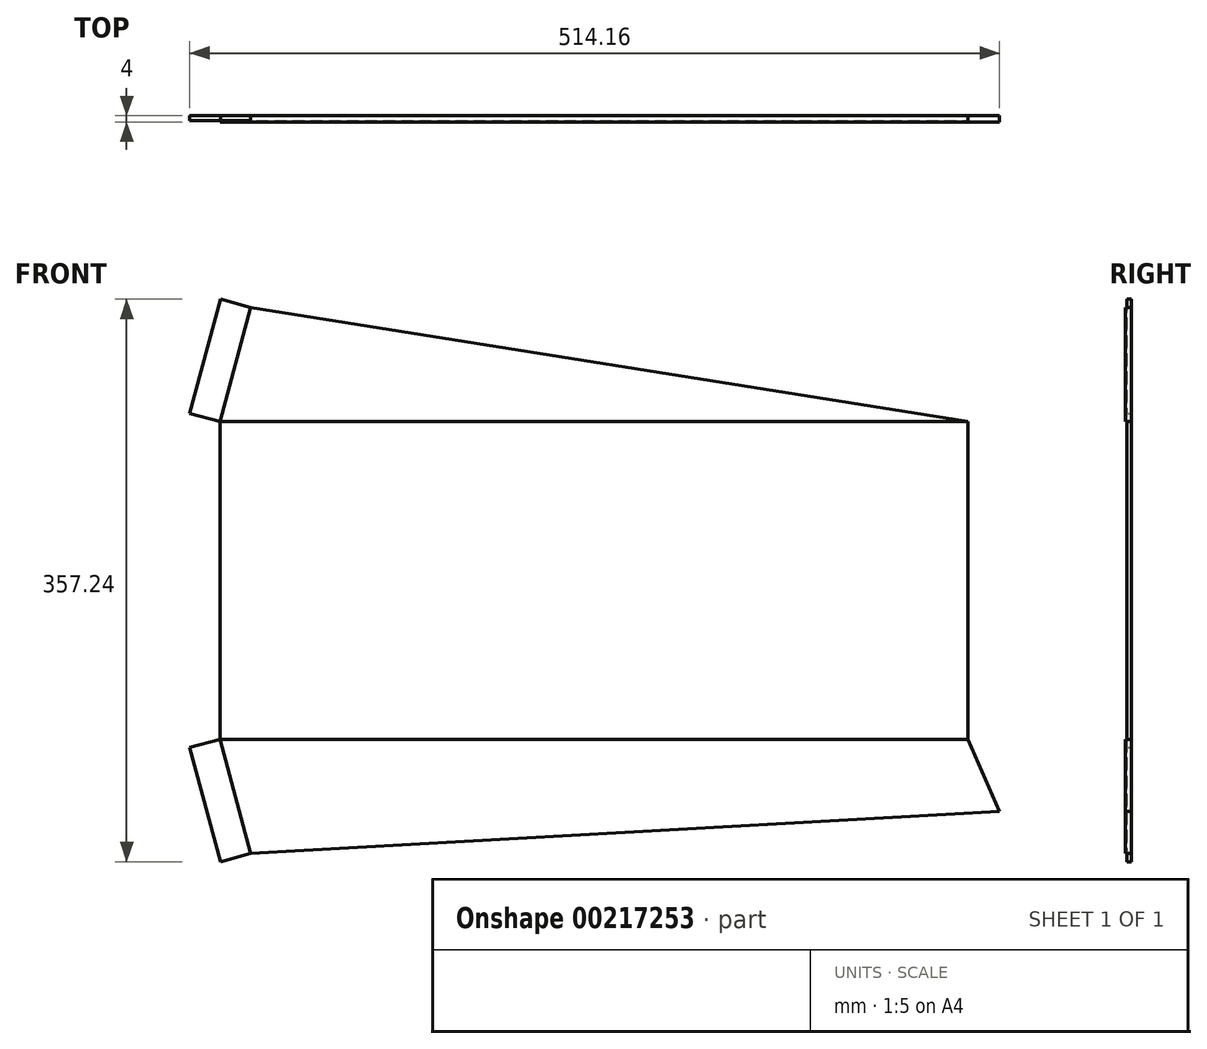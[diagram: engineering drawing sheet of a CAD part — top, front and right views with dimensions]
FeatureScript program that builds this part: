
annotation { "Feature Type Name" : "Feature", "Feature Type Description" : "" }
export const myFeature = defineFeature(function(context is Context, id is Id, definition is map)
    precondition{}
    {
        {
            var Q0;
            Q0=qCreatedBy(makeId("Front.planeOp"),FACE);
            var sketch = newSketch(context, id + "F0", { "sketchPlane" : qUnion([Q0])});
            skLineSegment(sketch, "E0.bottom", {"start": v(-237.5, 101) * mm, "end": v(237.5, 101) * mm});
            skLineSegment(sketch, "E0.top", {"start": v(-237.5, -101) * mm, "end": v(237.5, -101) * mm});
            skLineSegment(sketch, "E0.left", {"start": v(-237.5, 101) * mm, "end": v(-237.5, -101) * mm});
            skLineSegment(sketch, "E0.right", {"start": v(237.5, 101) * mm, "end": v(237.5, -101) * mm});
            skPoint(sketch, "E0.middle", {"position": v(0, 0) * mm});
            skLineSegment(sketch, "E1", {"start": v(237.5, 101) * mm, "end": v(-218.09, 173.44) * mm});
            skLineSegment(sketch, "E2", {"start": v(-237.5, 101) * mm, "end": v(-218.09, 173.44) * mm});
            skLineSegment(sketch, "E3", {"start": v(0, 0) * mm, "end": v(122.53, 0) * mm});
            skLineSegment(sketch, "E4.MirrorCS", {"start": v(-237.5, -101) * mm, "end": v(-218.09, -173.44) * mm});
            skLineSegment(sketch, "E5", {"start": v(-218.09, 173.44) * mm, "end": v(-237.4, 178.62) * mm});
            skLineSegment(sketch, "E6", {"start": v(-237.4, 178.62) * mm, "end": v(-256.82, 106.18) * mm});
            skLineSegment(sketch, "E7", {"start": v(-237.5, 101) * mm, "end": v(-256.82, 106.18) * mm});
            skLineSegment(sketch, "E8.MirrorCS", {"start": v(-237.4, -178.62) * mm, "end": v(-256.82, -106.18) * mm});
            skLineSegment(sketch, "E9.MirrorCS", {"start": v(-218.09, -173.44) * mm, "end": v(-237.4, -178.62) * mm});
            skLineSegment(sketch, "E10.MirrorCS", {"start": v(-237.5, -101) * mm, "end": v(-256.82, -106.18) * mm});
            skLineSegment(sketch, "E11", {"start": v(237.5, -101) * mm, "end": v(257.34, -146.54) * mm});
            skLineSegment(sketch, "E12", {"start": v(257.34, -146.54) * mm, "end": v(-218.09, -173.44) * mm});
            skLineSegment(sketch, "E13", {"start": v(237.5, -101) * mm, "end": v(305.35, -101) * mm});
            skSolve(sketch);
        }
        {
            var Q0;
            Q0=makeQuery(id+"F0.imprint","IMPRINT",FACE,{"disambiguationData":[TD([[makeQuery(id+"F0.imprint","IMPRINT",EDGE,{"derivedFrom":sQuery(id+"F0.wireOp",EDGE,"E0.bottom")}),1.0]])]});
            var Q1;
            Q1=makeQuery(id+"F0.imprint","IMPRINT",FACE,{"disambiguationData":[TD([[makeQuery(id+"F0.imprint","IMPRINT",EDGE,{"derivedFrom":sQuery(id+"F0.wireOp",EDGE,"E0.top")}),-1.0]])]});
            var Q2;
            Q2=makeQuery(id+"F0.imprint","IMPRINT",FACE,{"disambiguationData":[TD([[makeQuery(id+"F0.imprint","IMPRINT",EDGE,{"derivedFrom":sQuery(id+"F0.wireOp",EDGE,"5Q2M1Ocz-YDhd-RXOH-hbY3-pgjBZuunluBV.bottom")}),-1.0]])]});
            var Q3;
            Q3=makeQuery(id+"F0.imprint","IMPRINT",FACE,{"disambiguationData":[TD([[makeQuery(id+"F0.imprint","IMPRINT",EDGE,{"derivedFrom":sQuery(id+"F0.wireOp",EDGE,"7lXgpmdG-1jMo-cuFY-4l7G-SptWCp1jjVzk.bottom")}),-1.0]])]});
            extrude(context, id + "F1", {"entities" : qUnion([Q0, Q1, Q2, Q3]), "depth" : 4 * mm});
        }
        {
            var Q0;
            Q0=makeQuery(id+"F0.imprint","IMPRINT",FACE,{"disambiguationData":[TD([[makeQuery(id+"F0.imprint","IMPRINT",EDGE,{"derivedFrom":sQuery(id+"F0.wireOp",EDGE,"E0.bottom")}),-1.0]])]});
            var Q1;
            Q1=makeQuery(id+"F0.imprint","IMPRINT",FACE,{"disambiguationData":[TD([[makeQuery(id+"F0.imprint","IMPRINT",EDGE,{"derivedFrom":sQuery(id+"F0.wireOp",EDGE,"E2")}),1.0]])]});
            var Q2;
            Q2=makeQuery(id+"F0.imprint","IMPRINT",FACE,{"disambiguationData":[TD([[makeQuery(id+"F0.imprint","IMPRINT",EDGE,{"derivedFrom":sQuery(id+"F0.wireOp",EDGE,"E4.MirrorCS")}),-1.0]])]});
            extrude(context, id + "F2", {"entities" : qUnion([Q0, Q1, Q2]), "depth" : 3 * mm});
        }
    });
